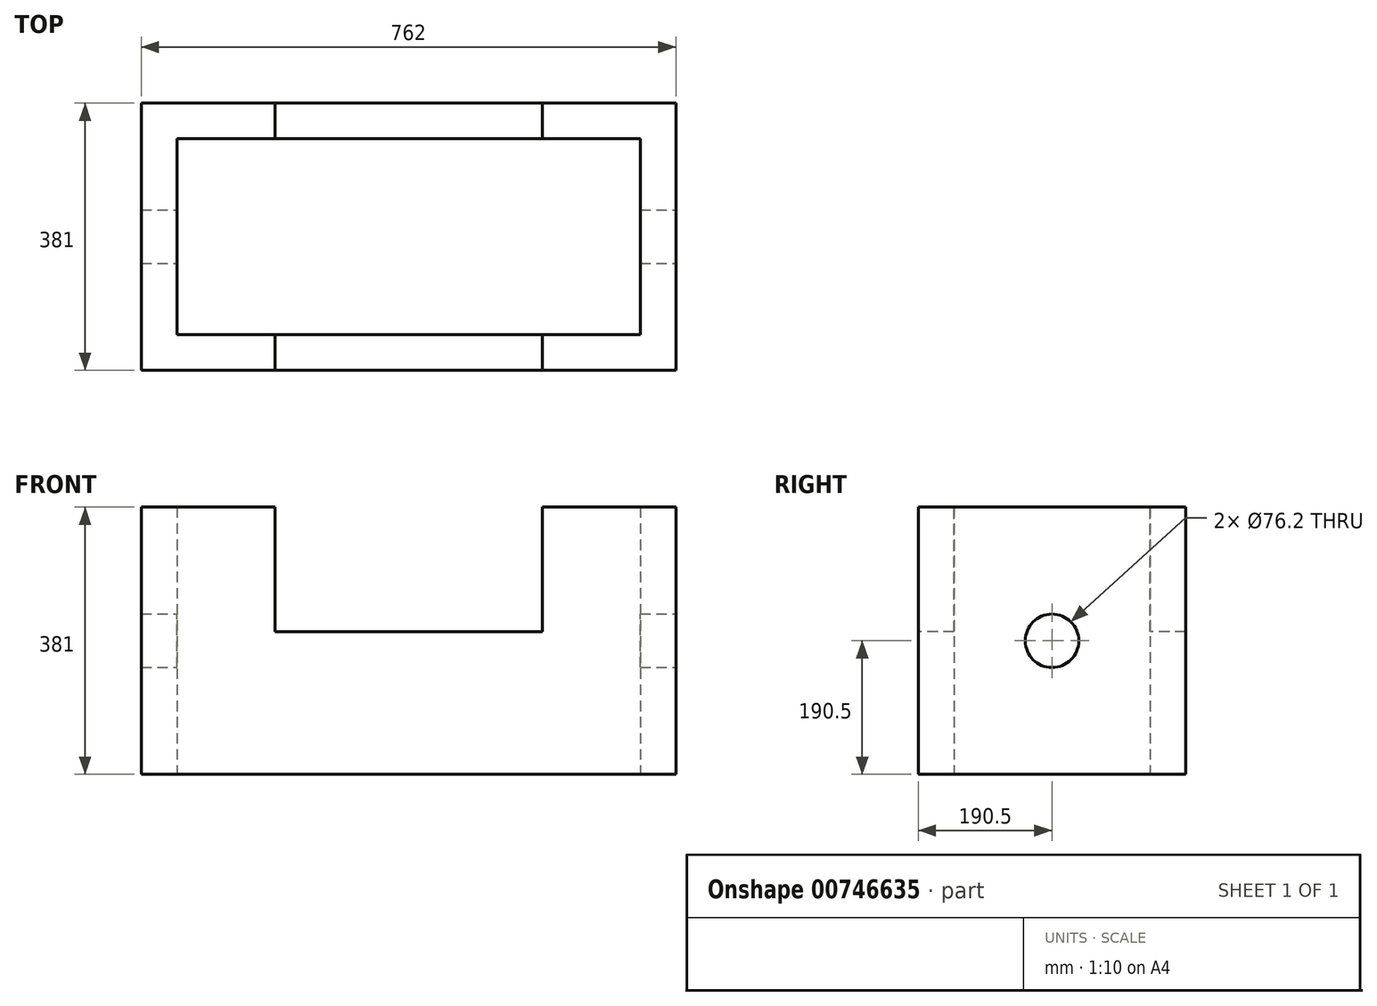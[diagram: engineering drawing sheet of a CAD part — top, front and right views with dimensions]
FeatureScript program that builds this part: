
annotation { "Feature Type Name" : "Feature", "Feature Type Description" : "" }
export const myFeature = defineFeature(function(context is Context, id is Id, definition is map)
    precondition{}
    {
        {
            var Q0;
            Q0=qCreatedBy(makeId("Top.planeOp"),FACE);
            var sketch = newSketch(context, id + "F0", { "sketchPlane" : qUnion([Q0])});
            skLineSegment(sketch, "E0.bottom", {"start": v(-381, 190.5) * mm, "end": v(381, 190.5) * mm});
            skLineSegment(sketch, "E0.top", {"start": v(-381, -190.5) * mm, "end": v(381, -190.5) * mm});
            skLineSegment(sketch, "E0.left", {"start": v(-381, 190.5) * mm, "end": v(-381, -190.5) * mm});
            skLineSegment(sketch, "E0.right", {"start": v(381, 190.5) * mm, "end": v(381, -190.5) * mm});
            skLineSegment(sketch, "E1.bottom", {"start": v(-330.2, 139.7) * mm, "end": v(330.2, 139.7) * mm});
            skLineSegment(sketch, "E1.top", {"start": v(-330.2, -139.7) * mm, "end": v(330.2, -139.7) * mm});
            skLineSegment(sketch, "E1.left", {"start": v(-330.2, 139.7) * mm, "end": v(-330.2, -139.7) * mm});
            skLineSegment(sketch, "E1.right", {"start": v(330.2, 139.7) * mm, "end": v(330.2, -139.7) * mm});
            skSolve(sketch);
        }
        {
            var Q0;
            Q0=makeQuery(id+"F0.imprint","IMPRINT",FACE,{"disambiguationData":[TD([[makeQuery(id+"F0.imprint","IMPRINT",EDGE,{"derivedFrom":sQuery(id+"F0.wireOp",EDGE,"E0.bottom")}),-1.0]])]});
            extrude(context, id + "F1", {"entities" : qUnion([Q0]), "depth" : 381 * mm, "offsetDistance" : 25.4 * mm});
        }
        {
            var Q0;
            Q0=makeQuery(id+"F1.opExtrude","SWEPT_FACE",FACE,{"disambiguationData":[OSD([sQuery(id+"F0.wireOp",EDGE,"E0.top")])]});
            var sketch = newSketch(context, id + "F2", { "sketchPlane" : qUnion([Q0])});
            skLineSegment(sketch, "E2.bottom", {"start": v(-190.5, 381) * mm, "end": v(190.5, 381) * mm});
            skLineSegment(sketch, "E2.top", {"start": v(-190.5, 203.2) * mm, "end": v(190.5, 203.2) * mm});
            skLineSegment(sketch, "E2.left", {"start": v(-190.5, 381) * mm, "end": v(-190.5, 203.2) * mm});
            skLineSegment(sketch, "E2.right", {"start": v(190.5, 381) * mm, "end": v(190.5, 203.2) * mm});
            skSolve(sketch);
        }
        {
            var Q0;
            Q0=makeQuery(id+"F2.imprint","IMPRINT",FACE,{"disambiguationData":[TD([[makeQuery(id+"F2.imprint","IMPRINT",EDGE,{"derivedFrom":sQuery(id+"F2.wireOp",EDGE,"E2.bottom")}),-1.0]])]});
            extrude(context, id + "F3", {"entities" : qUnion([Q0]), "operationType" : NewBodyOperationType.REMOVE, "oppositeDirection" : true, "depth" : 1270 * mm, "offsetDistance" : 25.4 * mm});
        }
        {
            var Q0;
            Q0=makeQuery(id+"F1.opExtrude","SWEPT_FACE",FACE,{"disambiguationData":[OSD([sQuery(id+"F0.wireOp",EDGE,"E0.right")])]});
            var sketch = newSketch(context, id + "F4", { "sketchPlane" : qUnion([Q0])});
            skCircle(sketch, "E3", {"center": v(0, 190.5) * mm, "radius": 38.1 * mm});
            skSolve(sketch);
        }
        {
            var Q0;
            Q0=makeQuery(id+"F4.imprint","IMPRINT",FACE,{"disambiguationData":[TD([[makeQuery(id+"F4.imprint","IMPRINT",EDGE,{"derivedFrom":sQuery(id+"F4.wireOp",EDGE,"E3")}),1.0]])]});
            extrude(context, id + "F5", {"entities" : qUnion([Q0]), "operationType" : NewBodyOperationType.REMOVE, "oppositeDirection" : true, "depth" : 1270 * mm, "offsetDistance" : 25.4 * mm});
        }
    });
